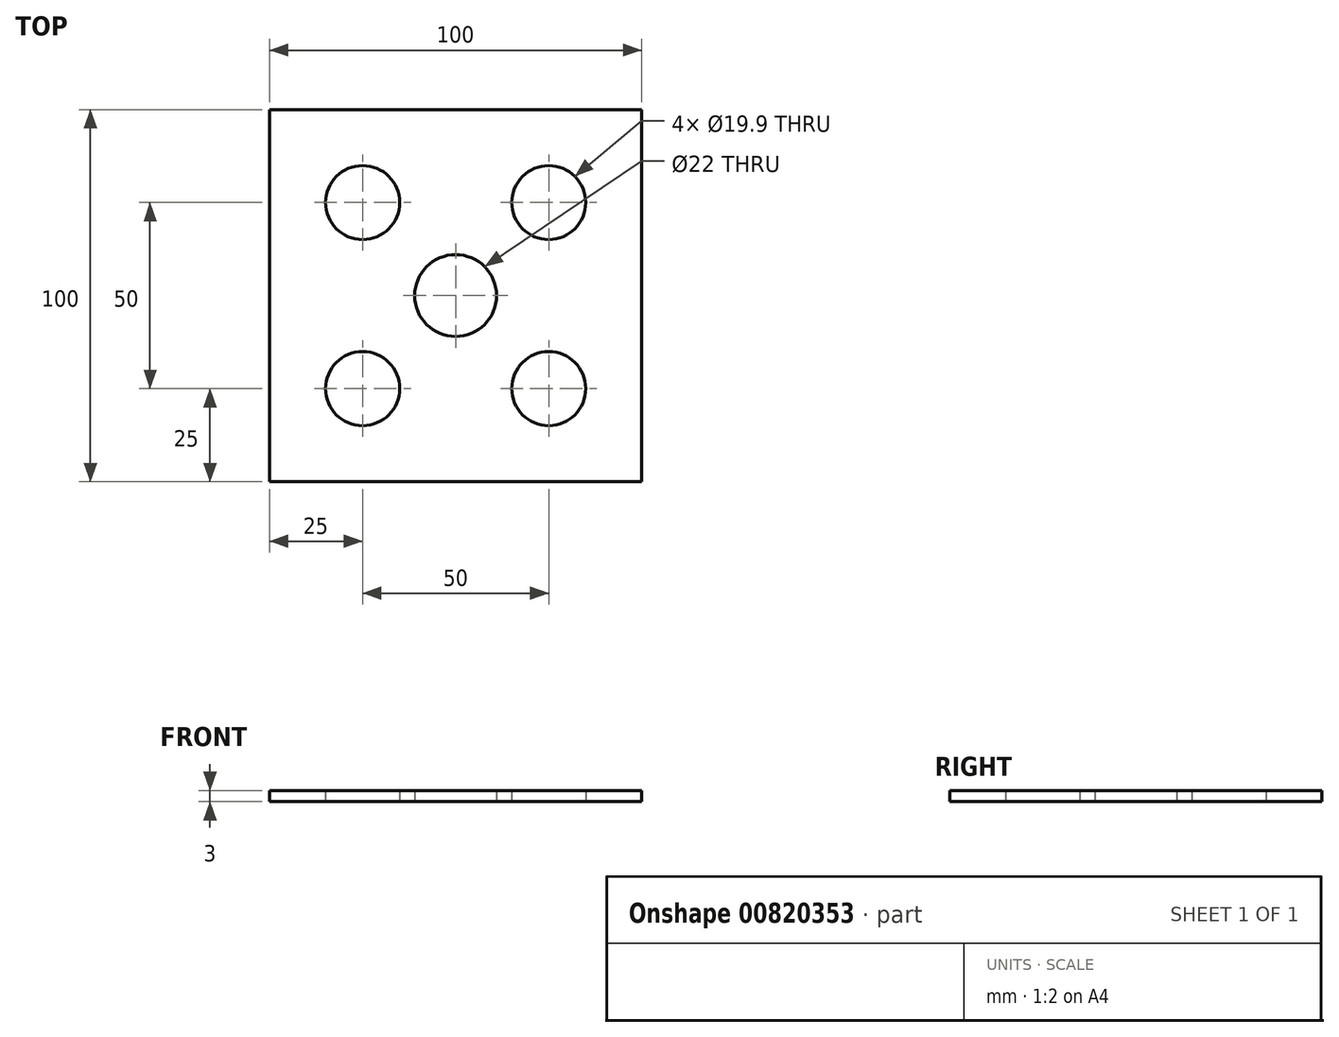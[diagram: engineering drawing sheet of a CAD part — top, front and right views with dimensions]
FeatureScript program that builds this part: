
annotation { "Feature Type Name" : "Feature", "Feature Type Description" : "" }
export const myFeature = defineFeature(function(context is Context, id is Id, definition is map)
    precondition{}
    {
        {
            var Q0;
            Q0=qCreatedBy(makeId("Top.planeOp"),FACE);
            var sketch = newSketch(context, id + "F0", { "sketchPlane" : qUnion([Q0])});
            skCircle(sketch, "E0", {"center": v(0, 0) * mm, "radius": 11 * mm});
            skLineSegment(sketch, "E1", {"start": v(0, 50) * mm, "end": v(50, 50) * mm});
            skLineSegment(sketch, "E2", {"start": v(50, 50) * mm, "end": v(50, -50) * mm});
            skLineSegment(sketch, "E3", {"start": v(50, -50) * mm, "end": v(-50, -50) * mm});
            skLineSegment(sketch, "E4", {"start": v(-50, -50) * mm, "end": v(-50, 50) * mm});
            skLineSegment(sketch, "E5", {"start": v(-50, 50) * mm, "end": v(0, 50) * mm});
            skCircle(sketch, "E6", {"center": v(-25, 25) * mm, "radius": 9.95 * mm});
            skCircle(sketch, "E7", {"center": v(25, 25) * mm, "radius": 9.95 * mm});
            skCircle(sketch, "E8", {"center": v(25, -25) * mm, "radius": 9.95 * mm});
            skCircle(sketch, "E9", {"center": v(-25, -25) * mm, "radius": 9.95 * mm});
            skPoint(sketch, "E10.start.orphan", {"position": v(-50, 0) * mm});
            skPoint(sketch, "E11.orphan", {"position": v(0, -50) * mm});
            skPoint(sketch, "E12.end.orphan", {"position": v(50, 0) * mm});
            skSolve(sketch);
        }
        {
            var Q0;
            Q0 = qSketchRegion(id + "F0", true);
            extrude(context, id + "F1", {"entities" : qUnion([Q0]), "depth" : 3 * mm, "offsetDistance" : 25 * mm});
        }
    });
